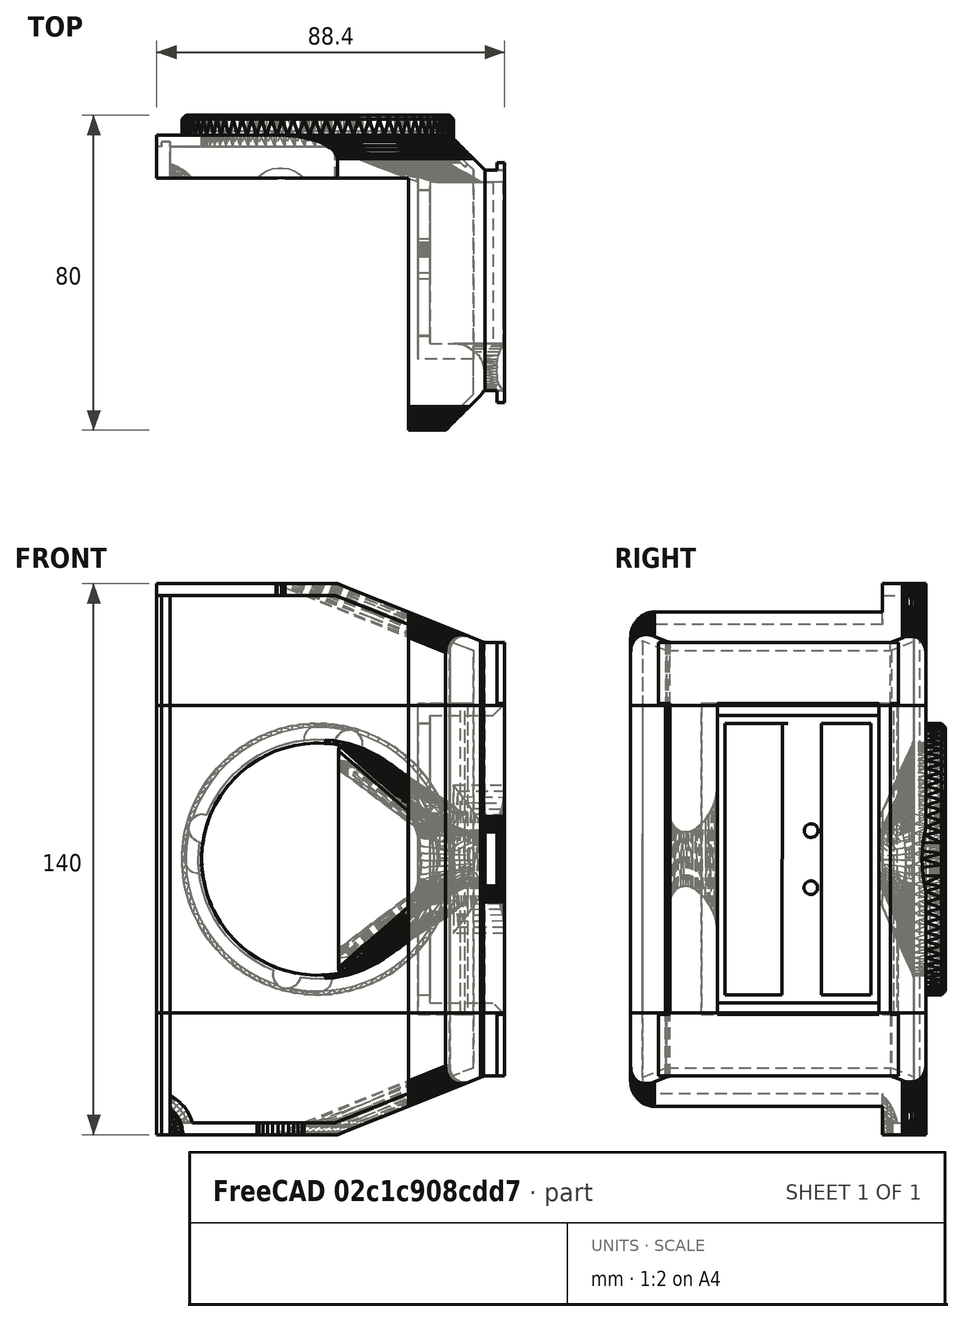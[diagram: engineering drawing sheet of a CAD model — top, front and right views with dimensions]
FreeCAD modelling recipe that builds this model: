
FCSTD DOCUMENT  (FreeCAD 0.19R24267 +148 (Git))
Label: FED feeder
License: All rights reserved
LicenseURL: http://en.wikipedia.org/wiki/All_rights_reserved
objects: Part::Box×3, Part::Cut×3, PartDesign::FeatureBase×3, PartDesign::Body×3, Part::Feature×1
note: 13 computed .brp shape members not serialized (recipe doc carries the construction recipe); baked Part::Feature solids carry a one-line shape summary decoded from their .brp

FEATURE [Part::Feature] FED_Base001_solid  label="FED_Base001 (Solid)"
  shape: bbox 88.95 x 80.55 x 140.6 mm, 9292 faces (baked)
FEATURE [Part::Box] Box  label="Cube"
  AttacherType = Attacher::AttachEngine3D
  Height = 150
  Length = 105
  Placement = pos=(-87,-1,-73) rot=(0,0,1;0rad)
  Width = 65
  expr: Length = 105mm
FEATURE [Part::Cut] Cut
  Base = -> FED_Base001_solid
  Tool = -> Box
FEATURE [PartDesign::FeatureBase] BaseFeature
  BaseFeature = -> Cut
FEATURE [PartDesign::Body] Body
  BaseFeature = -> Cut
  Group = -> [BaseFeature]
  Origin = -> Origin
  Tip = -> BaseFeature
FEATURE [Part::Box] Box001  label="Cube001"
  AttacherType = Attacher::AttachEngine3D
  Height = 40
  Length = 95
  Placement = pos=(-47,-1,-79) rot=(0,0,1;0rad)
  Width = 80
FEATURE [Part::Box] Box002  label="Cube002"
  AttacherType = Attacher::AttachEngine3D
  Height = 40
  Length = 95
  Placement = pos=(-47,-1,39) rot=(0,0,1;0rad)
  Width = 80
FEATURE [Part::Cut] Cut001
  Base = -> BaseFeature
  Tool = -> Box001
FEATURE [PartDesign::FeatureBase] BaseFeature001
  BaseFeature = -> Cut001
FEATURE [PartDesign::Body] Body001
  BaseFeature = -> Cut001
  Group = -> [BaseFeature001]
  Origin = -> Origin001
  Tip = -> BaseFeature001
FEATURE [Part::Cut] Cut002
  Base = -> BaseFeature001
  Tool = -> Box002
FEATURE [PartDesign::FeatureBase] BaseFeature002
  BaseFeature = -> Cut002
FEATURE [PartDesign::Body] Body002
  BaseFeature = -> Cut002
  Group = -> [BaseFeature002]
  Origin = -> Origin002
  Tip = -> BaseFeature002
